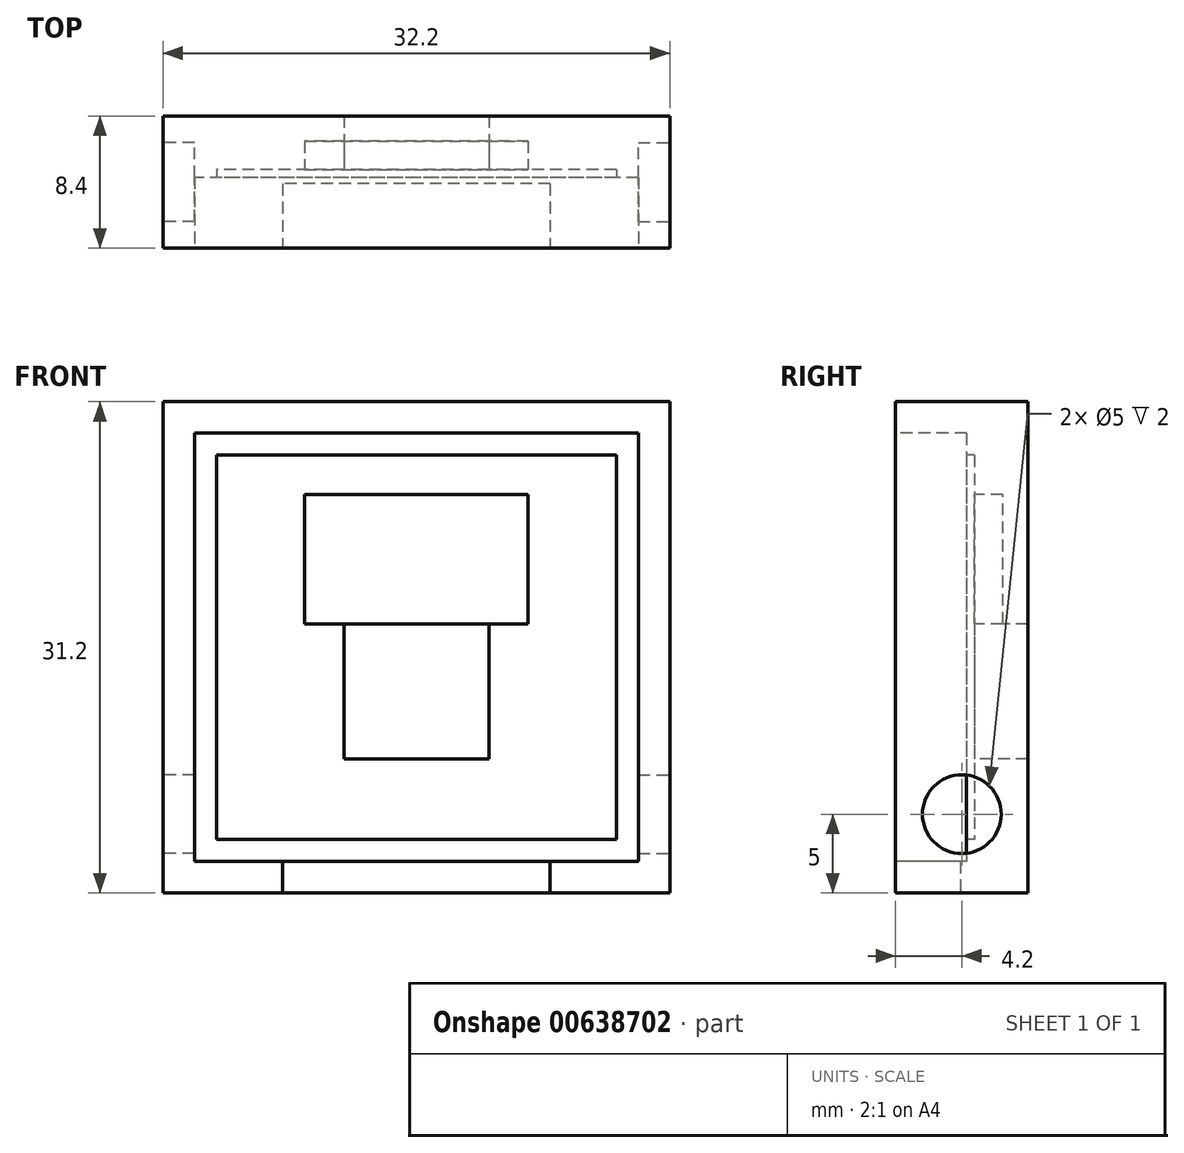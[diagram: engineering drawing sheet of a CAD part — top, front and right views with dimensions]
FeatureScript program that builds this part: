
annotation { "Feature Type Name" : "Feature", "Feature Type Description" : "" }
export const myFeature = defineFeature(function(context is Context, id is Id, definition is map)
    precondition{}
    {
        {
            var Q0;
            Q0=qCreatedBy(makeId("Front.planeOp"),FACE);
            var sketch = newSketch(context, id + "F0", { "sketchPlane" : qUnion([Q0])});
            skLineSegment(sketch, "E0.bottom", {"start": v(16.1, 15.6) * mm, "end": v(-16.1, 15.6) * mm});
            skLineSegment(sketch, "E0.top", {"start": v(16.1, -15.6) * mm, "end": v(-16.1, -15.6) * mm});
            skLineSegment(sketch, "E0.left", {"start": v(16.1, 15.6) * mm, "end": v(16.1, -15.6) * mm});
            skLineSegment(sketch, "E0.right", {"start": v(-16.1, 15.6) * mm, "end": v(-16.1, -15.6) * mm});
            skPoint(sketch, "E0.middle", {"position": v(0, 0) * mm});
            skSolve(sketch);
        }
        {
            var Q0;
            Q0 = qSketchRegion(id + "F0", true);
            extrude(context, id + "F1", {"entities" : qUnion([Q0]), "endBound" : BoundingType.SYMMETRIC, "depth" : 8.4 * mm, "offsetDistance" : 25 * mm});
        }
        {
            var Q0;
            Q0=makeQuery(id+"F1.opExtrude","CAP_FACE",FACE,{"disambiguationData":[OSD([sQuery(id+"F0.wireOp",EDGE,"E0.bottom"),sQuery(id+"F0.wireOp",EDGE,"E0.top"),sQuery(id+"F0.wireOp",EDGE,"E0.left"),sQuery(id+"F0.wireOp",EDGE,"E0.right")])],"isStart":false});
            var sketch = newSketch(context, id + "F2", { "sketchPlane" : qUnion([Q0])});
            skLineSegment(sketch, "E1.0", {"start": v(14.1, 13.6) * mm, "end": v(-14.1, 13.6) * mm});
            skLineSegment(sketch, "E1.1", {"start": v(14.1, 13.6) * mm, "end": v(14.1, -13.6) * mm});
            skLineSegment(sketch, "E1.2", {"start": v(14.1, -13.6) * mm, "end": v(-14.1, -13.6) * mm});
            skLineSegment(sketch, "E1.3", {"start": v(-14.1, 13.6) * mm, "end": v(-14.1, -13.6) * mm});
            skLineSegment(sketch, "E2.0", {"start": v(12.7, 12.2) * mm, "end": v(-12.7, 12.2) * mm});
            skLineSegment(sketch, "E2.1", {"start": v(12.7, 12.2) * mm, "end": v(12.7, -12.2) * mm});
            skLineSegment(sketch, "E2.2", {"start": v(12.7, -12.2) * mm, "end": v(-12.7, -12.2) * mm});
            skLineSegment(sketch, "E2.3", {"start": v(-12.7, 12.2) * mm, "end": v(-12.7, -12.2) * mm});
            skLineSegment(sketch, "E3", {"start": v(-8.5, -13.6) * mm, "end": v(-8.5, -15.6) * mm});
            skLineSegment(sketch, "E4", {"start": v(8.5, -13.6) * mm, "end": v(8.5, -15.6) * mm});
            skLineSegment(sketch, "E5.bottom", {"start": v(-4.6, 1.5) * mm, "end": v(4.6, 1.5) * mm});
            skLineSegment(sketch, "E5.top", {"start": v(-4.6, -7.1) * mm, "end": v(4.6, -7.1) * mm});
            skLineSegment(sketch, "E5.left", {"start": v(-4.6, 1.5) * mm, "end": v(-4.6, -7.1) * mm});
            skLineSegment(sketch, "E5.right", {"start": v(4.6, 1.5) * mm, "end": v(4.6, -7.1) * mm});
            skLineSegment(sketch, "E6", {"start": v(-4.6, 1.5) * mm, "end": v(-7.1, 1.5) * mm});
            skLineSegment(sketch, "E7", {"start": v(4.6, 1.5) * mm, "end": v(7.1, 1.5) * mm});
            skLineSegment(sketch, "E8", {"start": v(-7.1, 1.5) * mm, "end": v(-7.1, 9.7) * mm});
            skLineSegment(sketch, "E9", {"start": v(7.1, 1.5) * mm, "end": v(7.1, 9.7) * mm});
            skLineSegment(sketch, "E10", {"start": v(-7.1, 9.7) * mm, "end": v(7.1, 9.7) * mm});
            skSolve(sketch);
        }
        {
            var Q0;
            Q0=makeQuery(id+"F2.imprint","IMPRINT",FACE,{"disambiguationData":[TD([[makeQuery(id+"F2.imprint","IMPRINT",EDGE,{"derivedFrom":sQuery(id+"F2.wireOp",EDGE,"E5.bottom")}),-1.0]])]});
            extrude(context, id + "F3", {"entities" : qUnion([Q0]), "operationType" : NewBodyOperationType.REMOVE, "endBound" : BoundingType.UP_TO_NEXT, "oppositeDirection" : true, "depth" : 25 * mm, "offsetDistance" : 25 * mm});
        }
        {
            var Q0;
            Q0=makeQuery(id+"F2.imprint","IMPRINT",FACE,{"disambiguationData":[TD([[makeQuery(id+"F2.imprint","IMPRINT",EDGE,{"derivedFrom":sQuery(id+"F2.wireOp",EDGE,"E1.0")}),1.0]])]});
            extrude(context, id + "F4", {"entities" : qUnion([Q0]), "operationType" : NewBodyOperationType.REMOVE, "oppositeDirection" : true, "depth" : 4.5 * mm, "offsetDistance" : 25 * mm});
        }
        {
            var Q0;
            Q0=makeQuery(id+"F4.boolean.opBoolean","SPLIT",FACE,{"disambiguationData":[TD([makeQuery(id+"F3.boolean.opBoolean","COPY",FACE,{"derivedFrom":makeQuery(id+"F3.opExtrude","SWEPT_FACE",FACE,{"disambiguationData":[OSD([sQuery(id+"F2.wireOp",EDGE,"E5.bottom")])]})})])],"derivedFrom":makeQuery(id+"F1.opExtrude","CAP_FACE",FACE,{"disambiguationData":[OSD([sQuery(id+"F0.wireOp",EDGE,"E0.bottom"),sQuery(id+"F0.wireOp",EDGE,"E0.top"),sQuery(id+"F0.wireOp",EDGE,"E0.left"),sQuery(id+"F0.wireOp",EDGE,"E0.right")])],"isStart":false})});
            extrude(context, id + "F5", {"entities" : qUnion([Q0]), "operationType" : NewBodyOperationType.REMOVE, "oppositeDirection" : true, "depth" : 5 * mm, "offsetDistance" : 25 * mm});
        }
        {
            var Q0;
            {var subQ0=sQuery(id+"F2.wireOp",EDGE,"E3");Q0=makeQuery(id+"F2.imprint","IMPRINT",FACE,{"disambiguationData":[TD([[makeQuery(id+"F2.imprint","IMPRINT",EDGE,{"derivedFrom":subQ0}),1.0]])]});}
            extrude(context, id + "F6", {"entities" : qUnion([Q0]), "operationType" : NewBodyOperationType.REMOVE, "oppositeDirection" : true, "depth" : 4.1 * mm, "offsetDistance" : 25 * mm});
        }
        {
            var Q0;
            Q0=makeQuery(id+"F2.imprint","IMPRINT",FACE,{"disambiguationData":[TD([[makeQuery(id+"F2.imprint","IMPRINT",EDGE,{"derivedFrom":sQuery(id+"F2.wireOp",EDGE,"E5.bottom")}),1.0]])]});
            extrude(context, id + "F7", {"entities" : qUnion([Q0]), "operationType" : NewBodyOperationType.REMOVE, "oppositeDirection" : true, "depth" : 6.8 * mm, "offsetDistance" : 25 * mm});
        }
        {
            var Q0;
            Q0=makeQuery(id+"F1.opExtrude","SWEPT_FACE",FACE,{"disambiguationData":[OSD([sQuery(id+"F0.wireOp",EDGE,"E0.left")])]});
            var sketch = newSketch(context, id + "F8", { "sketchPlane" : qUnion([Q0])});
            skCircle(sketch, "E11", {"center": v(0, -10.6) * mm, "radius": 2.5 * mm});
            skSolve(sketch);
        }
        {
            var Q0;
            Q0=makeQuery(id+"F8.imprint","IMPRINT",FACE,{"disambiguationData":[TD([[makeQuery(id+"F8.imprint","IMPRINT",EDGE,{"derivedFrom":sQuery(id+"F8.wireOp",EDGE,"E11")}),1.0]])]});
            extrude(context, id + "F9", {"entities" : qUnion([Q0]), "operationType" : NewBodyOperationType.REMOVE, "oppositeDirection" : true, "depth" : 2 * mm, "offsetDistance" : 25 * mm});
        }
        {
            var Q0;
            Q0=makeQuery(id+"F1.opExtrude","SWEPT_FACE",FACE,{"disambiguationData":[OSD([sQuery(id+"F0.wireOp",EDGE,"E0.right")])]});
            var sketch = newSketch(context, id + "F10", { "sketchPlane" : qUnion([Q0])});
            skCircle(sketch, "E12", {"center": v(0, -10.6) * mm, "radius": 2.5 * mm});
            skSolve(sketch);
        }
        {
            var Q0;
            Q0=makeQuery(id+"F10.imprint","IMPRINT",FACE,{"disambiguationData":[TD([[makeQuery(id+"F10.imprint","IMPRINT",EDGE,{"derivedFrom":sQuery(id+"F10.wireOp",EDGE,"E12")}),1.0]])]});
            extrude(context, id + "F11", {"entities" : qUnion([Q0]), "operationType" : NewBodyOperationType.REMOVE, "oppositeDirection" : true, "depth" : 2 * mm, "offsetDistance" : 25 * mm});
        }
    });
